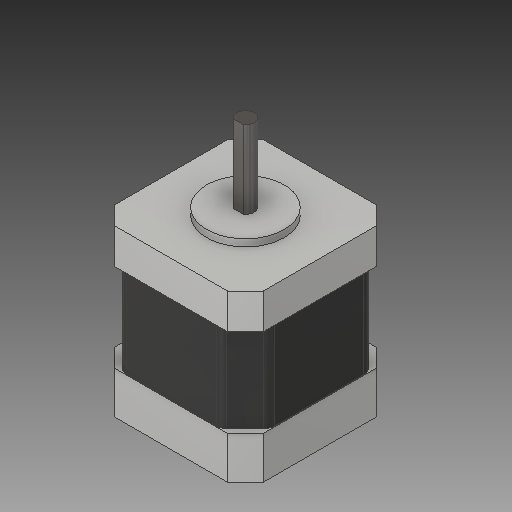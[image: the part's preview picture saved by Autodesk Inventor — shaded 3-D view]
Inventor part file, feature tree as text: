
AUTODESK INVENTOR PART (.ipt)
format: ipt  version: 2019 (Build 230136000, 136)  size: 227,840 bytes
history: native  units: mm
features: sketch x8, extrude x7, other x1, fillet x1, chamfer x1, projected_geometry x1
ambient origin geometry x8: Origin, YZ Plane, XZ Plane, XY Plane, X Axis, Y Axis, Z Axis, Center Point
bodies: Body1 (feature_tree)
feature tree (19):
  other  "Твердое тело1"
  extrude  "Выдавливание1"  Depth=42.3mm
  extrude  "Выдавливание2"  Depth=5.0mm
  extrude  "Выдавливание3"  Depth=5.0mm
  fillet  "Сопряжение1"  Radius=5.0mm
  extrude  "Выдавливание4"  Depth=5.0mm
  extrude  "Выдавливание5"  Depth=5.0mm
  extrude  "Выдавливание6"  Depth=5.0mm
  sketch  "Эскиз7"
  extrude  "Выдавливание8"  Depth=5.0mm
  chamfer  "Фаска1"  Distance=5.0mm
  sketch  "Эскиз1"
  sketch  "Эскиз2"
  sketch  "Эскиз3"
  projected_geometry  "Спроецированная петля1"
  sketch  "Эскиз4"
  sketch  "Эскиз5"
  sketch  "Эскиз6"
  sketch  "Эскиз9"
